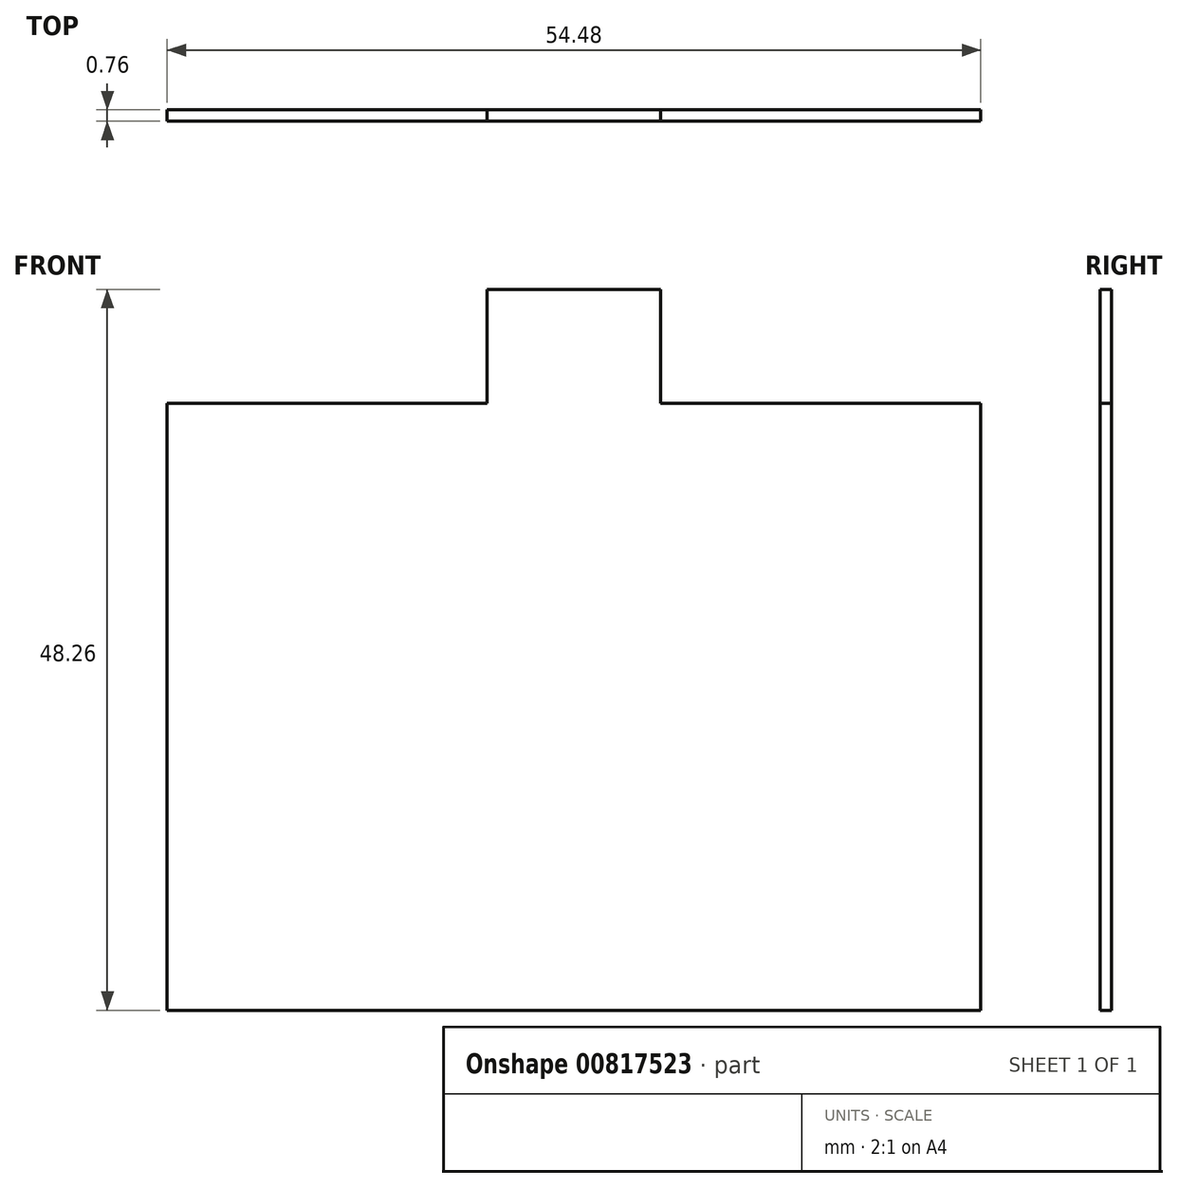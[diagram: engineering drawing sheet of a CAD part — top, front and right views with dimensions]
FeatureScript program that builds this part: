
annotation { "Feature Type Name" : "Feature", "Feature Type Description" : "" }
export const myFeature = defineFeature(function(context is Context, id is Id, definition is map)
    precondition{}
    {
        {
            var Q0;
            Q0=qCreatedBy(makeId("Top.planeOp"),FACE);
            var sketch = newSketch(context, id + "F0", { "sketchPlane" : qUnion([Q0])});
            skLineSegment(sketch, "E0.bottom", {"start": v(27.24, 0.38) * mm, "end": v(-27.24, 0.38) * mm});
            skLineSegment(sketch, "E0.top", {"start": v(27.24, -0.38) * mm, "end": v(-27.24, -0.38) * mm});
            skLineSegment(sketch, "E0.left", {"start": v(27.24, 0.38) * mm, "end": v(27.24, -0.38) * mm});
            skLineSegment(sketch, "E0.right", {"start": v(-27.24, 0.38) * mm, "end": v(-27.24, -0.38) * mm});
            skPoint(sketch, "E0.middle", {"position": v(0, 0) * mm});
            skLineSegment(sketch, "E1.bottom", {"start": v(5.8, 0.38) * mm, "end": v(-5.8, 0.38) * mm});
            skLineSegment(sketch, "E1.top", {"start": v(5.8, -0.38) * mm, "end": v(-5.8, -0.38) * mm});
            skLineSegment(sketch, "E1.left", {"start": v(5.8, 0.38) * mm, "end": v(5.8, -0.38) * mm});
            skLineSegment(sketch, "E1.right", {"start": v(-5.8, 0.38) * mm, "end": v(-5.8, -0.38) * mm});
            skSolve(sketch);
        }
        {
            var Q0;
            {var subQ2=sQuery(id+"F0.wireOp",EDGE,"E0.right");var subQ4=sQuery(id+"F0.wireOp",EDGE,"E0.left");Q0=qUnion([makeQuery(id+"F0.imprint","IMPRINT",FACE,{"disambiguationData":[TD([[makeQuery(id+"F0.imprint","IMPRINT",EDGE,{"derivedFrom":subQ4}),-1.0]])]}),makeQuery(id+"F0.imprint","IMPRINT",FACE,{"disambiguationData":[TD([[makeQuery(id+"F0.imprint","IMPRINT",EDGE,{"derivedFrom":subQ2}),1.0]])]})]);}
            extrude(context, id + "F1", {"entities" : qUnion([Q0]), "depth" : 40.64 * mm, "offsetDistance" : 25.4 * mm});
        }
        {
            var Q0;
            {var subQ2=sQuery(id+"F0.wireOp",EDGE,"E1.left");Q0=makeQuery(id+"F0.imprint","IMPRINT",FACE,{"disambiguationData":[TD([[makeQuery(id+"F0.imprint","IMPRINT",EDGE,{"derivedFrom":subQ2}),-1.0]])]});}
            extrude(context, id + "F2", {"entities" : qUnion([Q0]), "operationType" : NewBodyOperationType.ADD, "depth" : 48.26 * mm, "offsetDistance" : 25.4 * mm});
        }
    });
